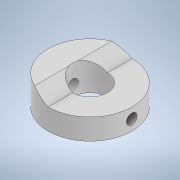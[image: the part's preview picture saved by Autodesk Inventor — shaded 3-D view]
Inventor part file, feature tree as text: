
AUTODESK INVENTOR PART (.ipt)
format: ipt  version: 2021 (Build 250183000, 183)  size: 141,824 bytes
history: native  units: mm
features: extrude x3, sketch x3, chamfer x2
ambient origin geometry x8: Origin, YZ Plane, XZ Plane, XY Plane, X Axis, Y Axis, Z Axis, Center Point
bodies: Solid1 (feature_tree)
feature tree (8):
  extrude  "Extrusion1"  Depth=8.3mm
  extrude  "Extrusion2"  TaperAngle=90.0deg  [1 undecoded]
  chamfer  "Chamfer4"  Distance=2.0mm
  chamfer  "Chamfer5"  Distance=4.0mm
  extrude  "Extrusion3"  Depth=2.5mm
  sketch  "Sketch1"  dims[d0=20.0mm d1=8.3mm]
  sketch  "Sketch2"  dims[d2=5.0mm d3=0.0mm d4=90.0deg d5=2.0mm d6=0.0mm d16=4.0mm d17=2.0mm d18=3.490659mm]
  sketch  "Sketch3"  dims[d19=4.0mm d20=2.0mm d21=3.490659mm d22=2.5mm d23=2.5mm d24=0.0mm d25=0.0mm]
note: 1 required parameter value undecoded (feature->parameter linkage not recoverable at this tier; creation-order binding heuristic only, values carry confidence <= 0.55)
